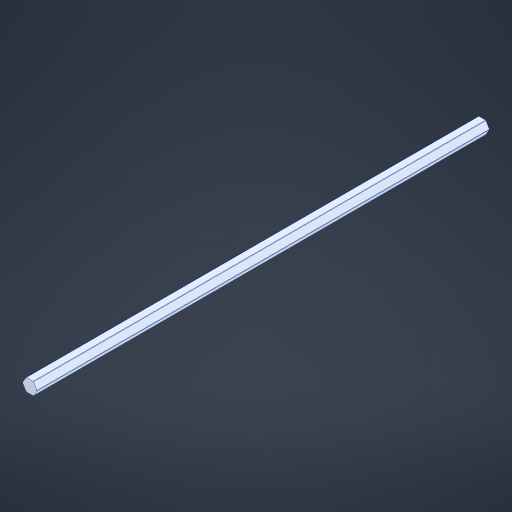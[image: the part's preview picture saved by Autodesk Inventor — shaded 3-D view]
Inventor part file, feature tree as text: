
AUTODESK INVENTOR PART (.ipt)
format: ipt  version: 2024 (Build 280153000, 153)  size: 201,216 bytes
history: native  units: in
note: dims shown in document units (in); Inventor stores cm internally (conversion verified against a paired STEP export)
features: fillet x1
ambient origin geometry x8: Origin, YZ Plane, XZ Plane, XY Plane, X Axis, Y Axis, Z Axis, Center Point
bodies: Solid1 (feature_tree)
feature tree (1):
  fillet  "Fillet1"  [1 undecoded]
note: 1 required parameter value undecoded (feature->parameter linkage not recoverable at this tier; creation-order binding heuristic only, values carry confidence <= 0.55)
